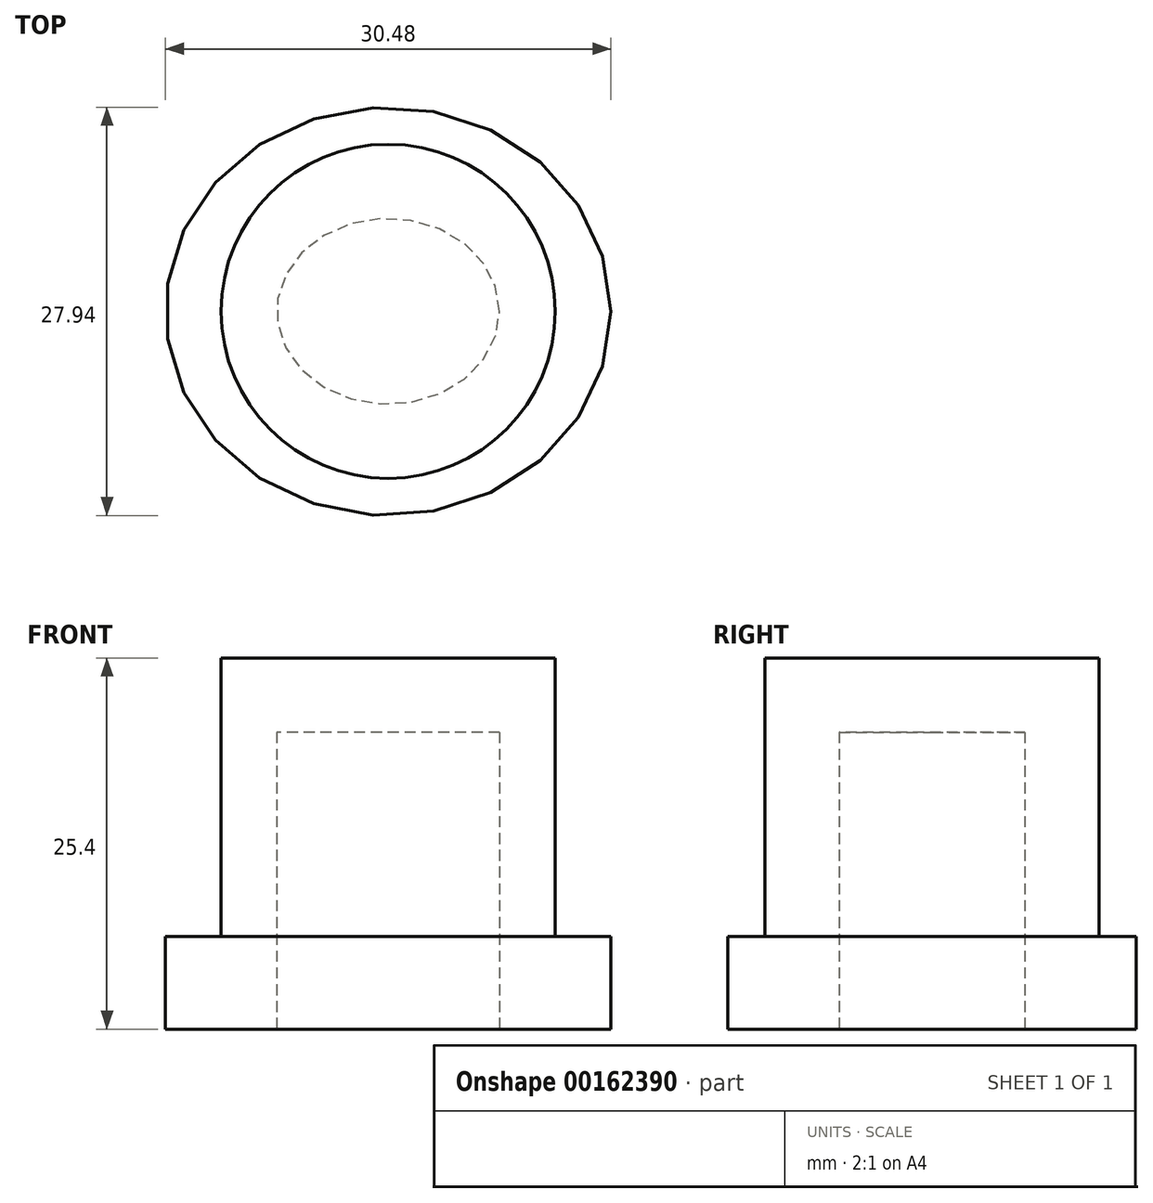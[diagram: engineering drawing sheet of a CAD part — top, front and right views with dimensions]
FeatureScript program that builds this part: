
annotation { "Feature Type Name" : "Feature", "Feature Type Description" : "" }
export const myFeature = defineFeature(function(context is Context, id is Id, definition is map)
    precondition{}
    {
        {
            var Q0;
            Q0=qCreatedBy(makeId("Top.planeOp"),FACE);
            var sketch = newSketch(context, id + "F0", { "sketchPlane" : qUnion([Q0])});
            skEllipse(sketch, "E0", {"center": v(0, 0) * mm, "majorRadius": 11.43 * mm, "minorRadius": 11.43 * mm, "majorAxis": v(-1, 0)});
            skEllipse(sketch, "E1", {"center": v(0, 0) * mm, "majorRadius": 15.24 * mm, "minorRadius": 13.97 * mm, "majorAxis": v(1, 0)});
            skEllipse(sketch, "E2", {"center": v(0, 0) * mm, "majorRadius": 7.62 * mm, "minorRadius": 6.35 * mm, "majorAxis": v(1, 0)});
            skSolve(sketch);
        }
        {
            var Q0;
            Q0=makeQuery(id+"F0.imprint","IMPRINT",FACE,{"disambiguationData":[TD([[makeQuery(id+"F0.imprint","IMPRINT",EDGE,{"derivedFrom":sQuery(id+"F0.wireOp",EDGE,"E0")}),1.0]])]});
            var Q1;
            Q1=makeQuery(id+"F0.imprint","IMPRINT",FACE,{"disambiguationData":[TD([[makeQuery(id+"F0.imprint","IMPRINT",EDGE,{"derivedFrom":sQuery(id+"F0.wireOp",EDGE,"E2")}),1.0]])]});
            extrude(context, id + "F1", {"entities" : qUnion([Q0, Q1]), "depth" : 25.4 * mm});
        }
        {
            var Q0;
            Q0=makeQuery(id+"F0.imprint","IMPRINT",FACE,{"disambiguationData":[TD([[makeQuery(id+"F0.imprint","IMPRINT",EDGE,{"derivedFrom":sQuery(id+"F0.wireOp",EDGE,"E0")}),-1.0]])]});
            extrude(context, id + "F2", {"entities" : qUnion([Q0]), "operationType" : NewBodyOperationType.ADD, "depth" : 6.35 * mm});
        }
        {
            var Q0;
            Q0=makeQuery(id+"F0.imprint","IMPRINT",FACE,{"disambiguationData":[TD([[makeQuery(id+"F0.imprint","IMPRINT",EDGE,{"derivedFrom":sQuery(id+"F0.wireOp",EDGE,"E2")}),1.0]])]});
            extrude(context, id + "F3", {"entities" : qUnion([Q0]), "operationType" : NewBodyOperationType.REMOVE, "depth" : 20.32 * mm});
        }
    });
